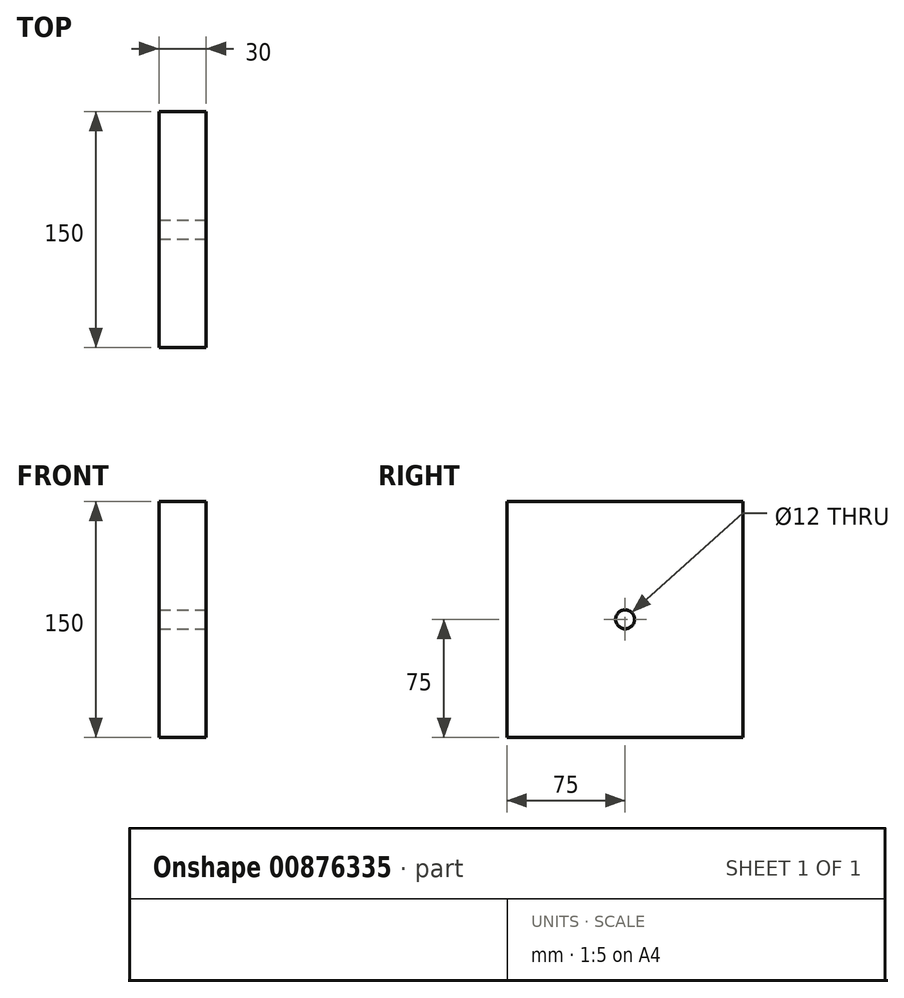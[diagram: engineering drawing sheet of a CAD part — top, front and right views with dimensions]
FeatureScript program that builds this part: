
annotation { "Feature Type Name" : "Feature", "Feature Type Description" : "" }
export const myFeature = defineFeature(function(context is Context, id is Id, definition is map)
    precondition{}
    {
        {
            var Q0;
            Q0=qCreatedBy(makeId("Front.planeOp"),FACE);
            var sketch = newSketch(context, id + "F0", { "sketchPlane" : qUnion([Q0])});
            skLineSegment(sketch, "E0", {"start": v(0, 0) * mm, "end": v(-30, 0) * mm});
            skLineSegment(sketch, "E1", {"start": v(-30, 0) * mm, "end": v(-30, 150) * mm});
            skLineSegment(sketch, "E2", {"start": v(-30, 150) * mm, "end": v(0, 150) * mm});
            skLineSegment(sketch, "E3", {"start": v(0, 150) * mm, "end": v(0, 0) * mm});
            skSolve(sketch);
        }
        {
            var Q0;
            Q0=qCreatedBy(makeId("Right.planeOp"),FACE);
            var sketch = newSketch(context, id + "F1", { "sketchPlane" : qUnion([Q0])});
            skLineSegment(sketch, "E4", {"start": v(0, 0) * mm, "end": v(-150, 0) * mm});
            skSolve(sketch);
        }
        {
            var Q0;
            Q0=makeQuery(id+"F0.imprint","IMPRINT",FACE,{"disambiguationData":[TD([[makeQuery(id+"F0.imprint","IMPRINT",EDGE,{"derivedFrom":sQuery(id+"F0.wireOp",EDGE,"E0")}),-1.0]])]});
            var Q1;
            Q1=sQuery(id+"F1.wireOp",EDGE,"E4");
            sweep(context, id + "F2", {"profiles" : qUnion([Q0]), "path" : qUnion([Q1])});
        }
        {
            var Q0;
            Q0=qCreatedBy(makeId("Right.planeOp"),FACE);
            var sketch = newSketch(context, id + "F3", { "sketchPlane" : qUnion([Q0])});
            skCircle(sketch, "E5", {"center": v(-75, 75) * mm, "radius": 12.75 * mm});
            skSolve(sketch);
        }
        {
            var Q0;
            Q0=sQuery(id+"F3.wireOp",VERTEX,"E5.center");
            var Q1;
            Q1=makeQuery(id+"F2.opSweep","SWEPT_BODY",BODY,{"disambiguationData":[OSD([sQuery(id+"F0.wireOp",EDGE,"E0"),sQuery(id+"F0.wireOp",EDGE,"E1"),sQuery(id+"F0.wireOp",EDGE,"E2"),sQuery(id+"F0.wireOp",EDGE,"E3"),sQuery(id+"F1.wireOp",EDGE,"E4")])]});
            hole(context, id + "F4", {"style" : HoleStyle.SIMPLE, "endStyle" : HoleEndStyle.THROUGH, "holeDiameter" : 12 * mm, "majorDiameter" : 5 * mm, "isTappedThrough" : true, "tappedDepth" : 12 * mm, "tapClearance" : 3, "locations" : qUnion([Q0]), "scope" : qUnion([Q1])});
        }
    });
